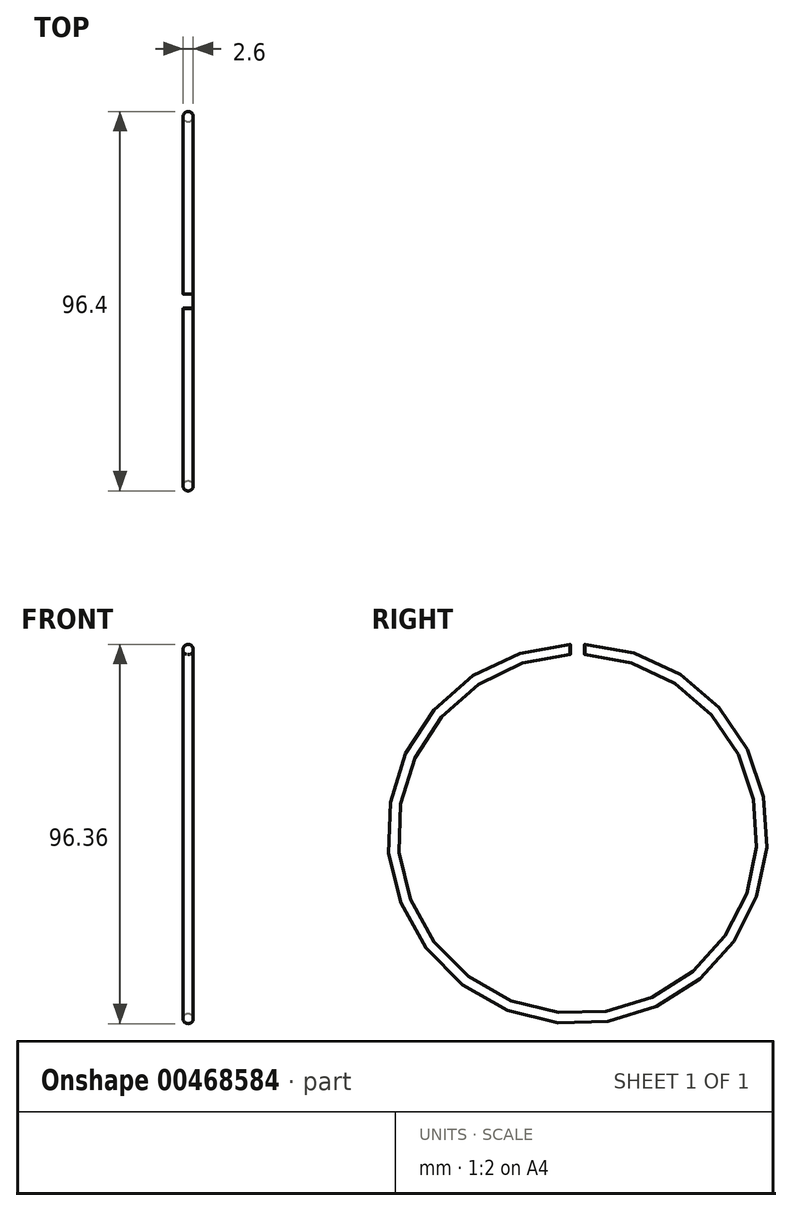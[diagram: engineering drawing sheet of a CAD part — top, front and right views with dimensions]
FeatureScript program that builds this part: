
annotation { "Feature Type Name" : "Feature", "Feature Type Description" : "" }
export const myFeature = defineFeature(function(context is Context, id is Id, definition is map)
    precondition{}
    {
        {
            var Q0;
            Q0=qCreatedBy(makeId("Front.planeOp"),FACE);
            var sketch = newSketch(context, id + "F0", { "sketchPlane" : qUnion([Q0])});
            skPoint(sketch, "E0", {"position": v(0, 46.9) * mm});
            skCircle(sketch, "E1", {"center": v(0, 46.9) * mm, "radius": 1.3 * mm});
            skLineSegment(sketch, "E2", {"start": v(0, 0) * mm, "end": v(4, 0) * mm, "construction": true});
            skSolve(sketch);
        }
        {
            var Q0;
            Q0 = qSketchRegion(id + "F0", true);
            var Q1;
            Q1=sQuery(id+"F0.wireOp",EDGE,"E2");
            revolve(context, id + "F1", {"entities" : qUnion([Q0]), "axis" : qUnion([Q1]), "revolveType" : RevolveType.FULL});
        }
        {
            var Q0;
            Q0=qCreatedBy(makeId("Right.planeOp"),FACE);
            var sketch = newSketch(context, id + "F2", { "sketchPlane" : qUnion([Q0])});
            skPoint(sketch, "E3", {"position": v(0, 46.9) * mm});
            skLineSegment(sketch, "E4.bottom", {"start": v(1.75, 48.4) * mm, "end": v(-1.75, 48.4) * mm});
            skLineSegment(sketch, "E4.top", {"start": v(1.75, 45.4) * mm, "end": v(-1.75, 45.4) * mm});
            skLineSegment(sketch, "E4.left", {"start": v(1.75, 48.4) * mm, "end": v(1.75, 45.4) * mm});
            skLineSegment(sketch, "E4.right", {"start": v(-1.75, 48.4) * mm, "end": v(-1.75, 45.4) * mm});
            skSolve(sketch);
        }
        {
            var Q0;
            Q0 = qSketchRegion(id + "F2", true);
            extrude(context, id + "F3", {"entities" : qUnion([Q0]), "operationType" : NewBodyOperationType.REMOVE, "oppositeDirection" : true, "depth" : 25 * mm, "offsetDistance" : 25 * mm, "symmetric" : true});
        }
        {
            var Q0;
            Q0=makeQuery(id+"F3.boolean.opBoolean","INTERSECT",EDGE,{"derivedFrom":[makeQuery(id+"F1.opRevolve","SWEPT_FACE",FACE,{"disambiguationData":[OSD([sQuery(id+"F0.wireOp",EDGE,"E1")])]}),makeQuery(id+"F3.opExtrude","SWEPT_FACE",FACE,{"disambiguationData":[OSD([sQuery(id+"F2.wireOp",EDGE,"E4.right")])]})]});
            var Q1;
            Q1=makeQuery(id+"F3.boolean.opBoolean","INTERSECT",EDGE,{"derivedFrom":[makeQuery(id+"F1.opRevolve","SWEPT_FACE",FACE,{"disambiguationData":[OSD([sQuery(id+"F0.wireOp",EDGE,"E1")])]}),makeQuery(id+"F3.opExtrude","SWEPT_FACE",FACE,{"disambiguationData":[OSD([sQuery(id+"F2.wireOp",EDGE,"E4.left")])]})]});
            chamfer(context, id + "F4", {"entities" : qUnion([Q0, Q1]), "width" : .1 * mm, "tangentPropagation" : true});
        }
    });
